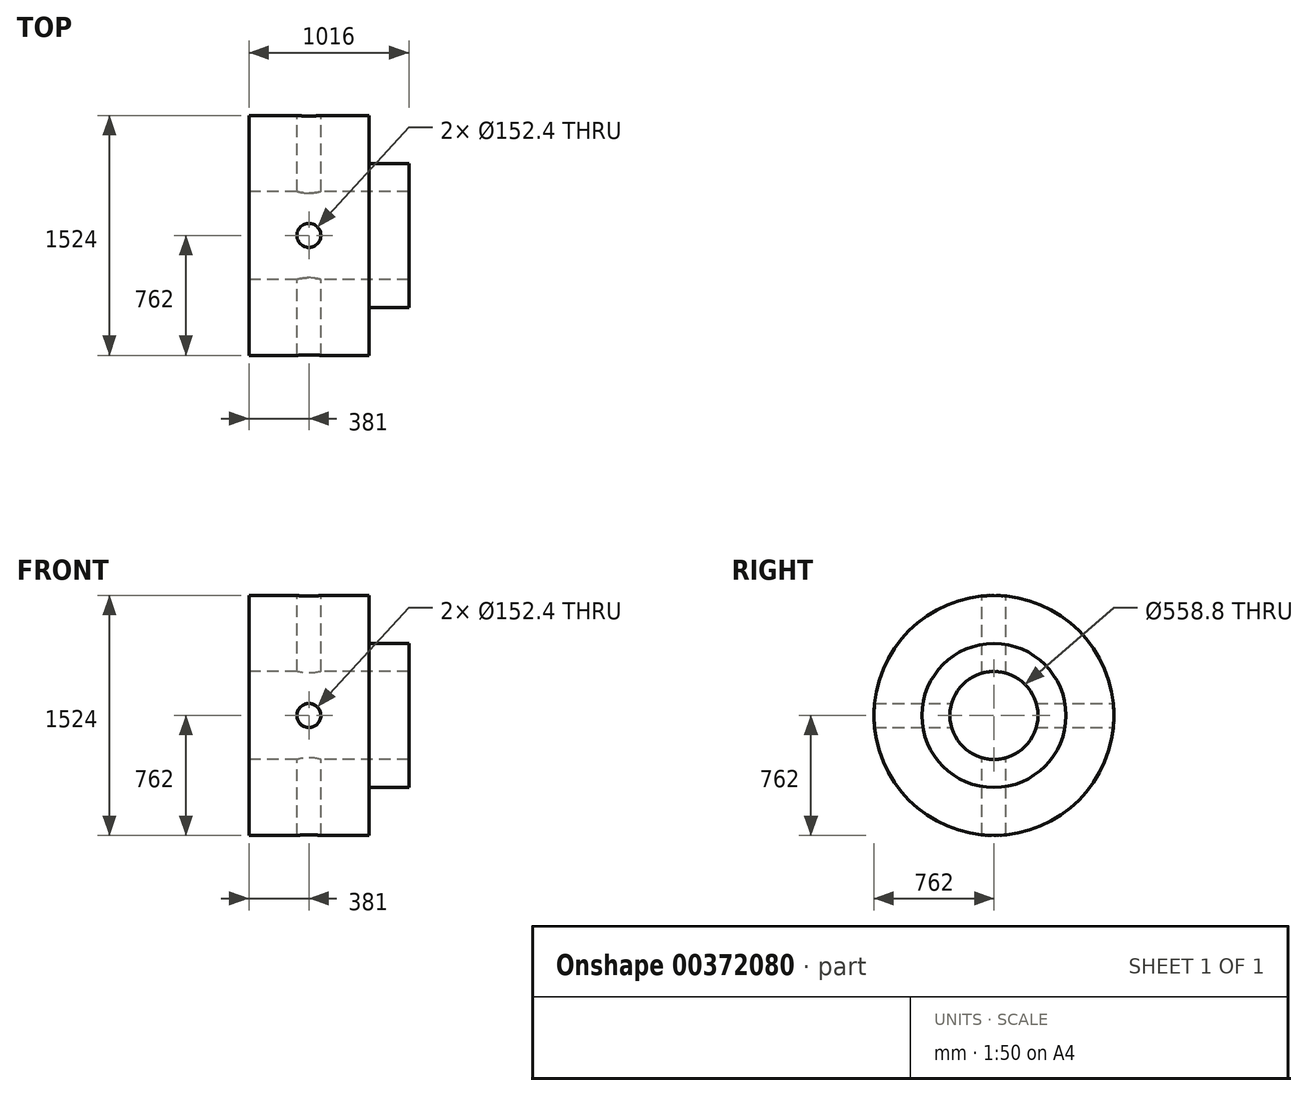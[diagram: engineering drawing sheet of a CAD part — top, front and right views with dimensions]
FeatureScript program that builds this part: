
annotation { "Feature Type Name" : "Feature", "Feature Type Description" : "" }
export const myFeature = defineFeature(function(context is Context, id is Id, definition is map)
    precondition{}
    {
        {
            var Q0;
            Q0=qCreatedBy(makeId("Front.planeOp"),FACE);
            var sketch = newSketch(context, id + "F0", { "sketchPlane" : qUnion([Q0])});
            skLineSegment(sketch, "E0", {"start": v(0, 762) * mm, "end": v(762, 762) * mm});
            skLineSegment(sketch, "E1", {"start": v(762, 762) * mm, "end": v(762, 457.2) * mm});
            skLineSegment(sketch, "E2", {"start": v(762, 457.2) * mm, "end": v(1016, 457.2) * mm});
            skLineSegment(sketch, "E3", {"start": v(1016, 457.2) * mm, "end": v(1016, 279.4) * mm});
            skLineSegment(sketch, "E4", {"start": v(1016, 279.4) * mm, "end": v(0, 279.4) * mm});
            skLineSegment(sketch, "E5", {"start": v(0, 279.4) * mm, "end": v(0, 762) * mm});
            skLineSegment(sketch, "E6", {"start": v(-55.75, 0) * mm, "end": v(1268.75, 0) * mm, "construction": true});
            skSolve(sketch);
        }
        {
            var Q0;
            Q0 = qSketchRegion(id + "F0", true);
            var Q1;
            Q1=sQuery(id+"F0.wireOp",EDGE,"E6");
            revolve(context, id + "F1", {"entities" : qUnion([Q0]), "axis" : qUnion([Q1]), "revolveType" : RevolveType.FULL});
        }
        {
            var Q0;
            Q0=qCreatedBy(makeId("Top.planeOp"),FACE);
            cPlane(context, id + "F2", {"entities" : qUnion([Q0]), "cplaneType" : CPlaneType.OFFSET, "offset" : 1524 * mm, "width" : 152.4 * mm, "height" : 152.4 * mm});
        }
        {
            var Q0;
            Q0=qCreatedBy(id+"F2.planeOp",FACE);
            var sketch = newSketch(context, id + "F3", { "sketchPlane" : qUnion([Q0])});
            skCircle(sketch, "E7", {"center": v(381, 0) * mm, "radius": 76.2 * mm});
            skSolve(sketch);
        }
        {
            var Q0;
            Q0 = qSketchRegion(id + "F3", true);
            extrude(context, id + "F4", {"entities" : qUnion([Q0]), "operationType" : NewBodyOperationType.REMOVE, "oppositeDirection" : true, "depth" : 2540 * mm});
        }
        {
            var Q0;
            Q0=qCreatedBy(makeId("Front.planeOp"),FACE);
            var sketch = newSketch(context, id + "F5", { "sketchPlane" : qUnion([Q0])});
            skCircle(sketch, "E8", {"center": v(381, 0) * mm, "radius": 76.2 * mm});
            skSolve(sketch);
        }
        {
            var Q0;
            Q0 = qSketchRegion(id + "F5", true);
            extrude(context, id + "F6", {"entities" : qUnion([Q0]), "operationType" : NewBodyOperationType.REMOVE, "endBound" : BoundingType.THROUGH_ALL, "depth" : 25.4 * mm, "hasSecondDirection" : true, "secondDirectionOppositeDirection" : true, "secondDirectionDepth" : 922.02 * mm});
        }
    });
